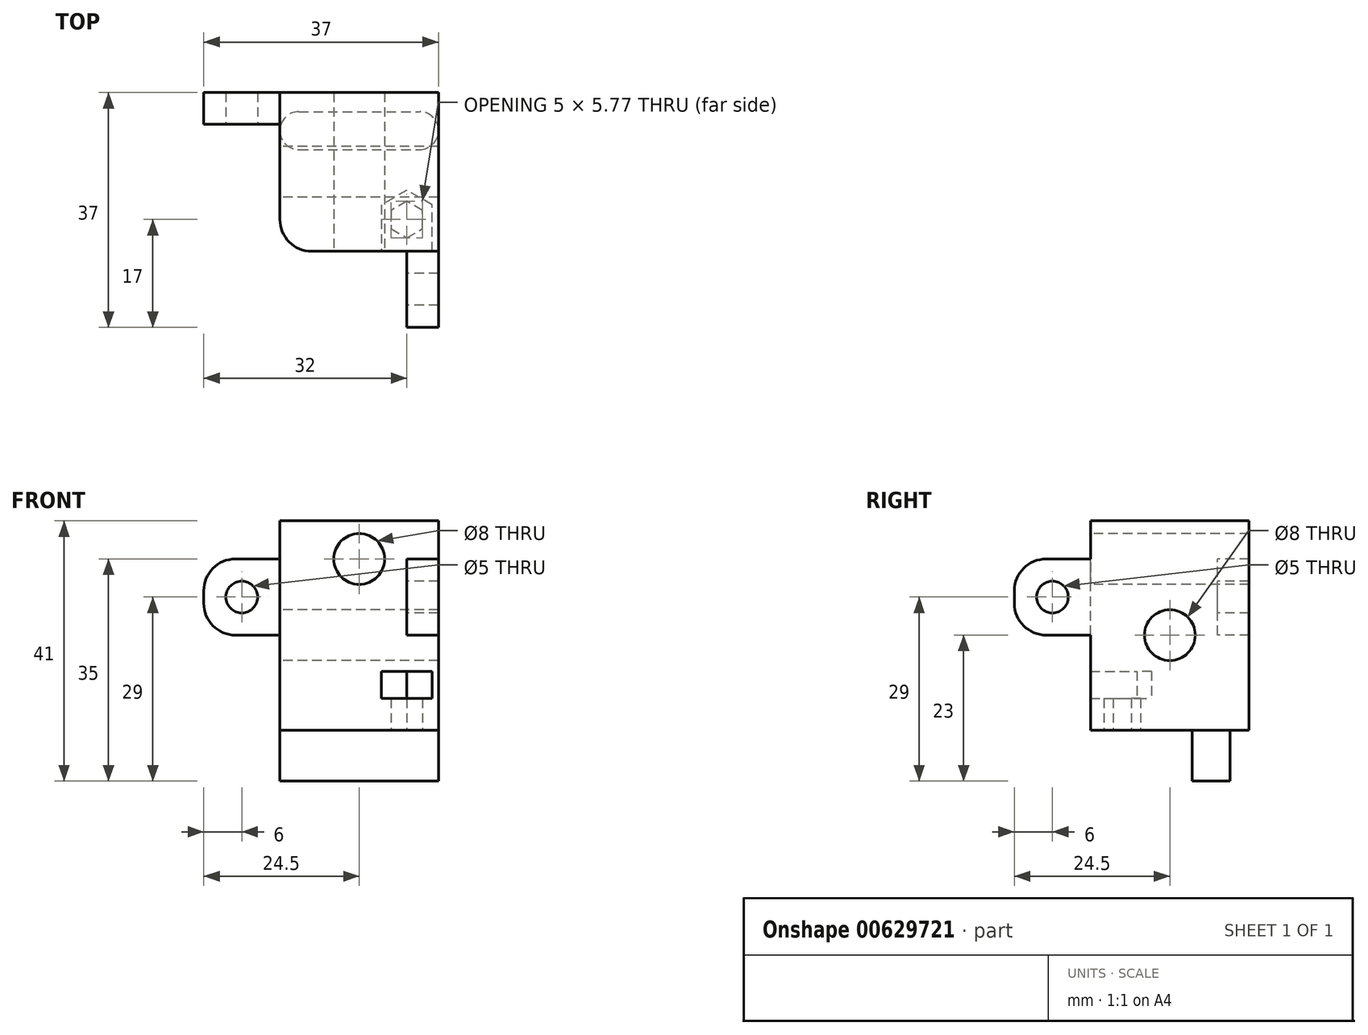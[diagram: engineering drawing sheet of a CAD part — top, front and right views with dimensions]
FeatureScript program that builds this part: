
annotation { "Feature Type Name" : "Feature", "Feature Type Description" : "" }
export const myFeature = defineFeature(function(context is Context, id is Id, definition is map)
    precondition{}
    {
        {
            var Q0;
            Q0=qCreatedBy(makeId("Front.planeOp"),FACE);
            var sketch = newSketch(context, id + "F0", { "sketchPlane" : qUnion([Q0])});
            skLineSegment(sketch, "E0.bottom", {"start": v(0, 0) * mm, "end": v(25, 0) * mm});
            skLineSegment(sketch, "E0.top", {"start": v(0, 45) * mm, "end": v(25, 45) * mm});
            skLineSegment(sketch, "E0.left", {"start": v(0, 0) * mm, "end": v(0, 45) * mm});
            skLineSegment(sketch, "E0.right", {"start": v(25, 0) * mm, "end": v(25, 45) * mm});
            skSolve(sketch);
        }
        {
            var Q0;
            Q0=makeQuery(id+"F0.imprint","IMPRINT",FACE,{"disambiguationData":[TD([[makeQuery(id+"F0.imprint","IMPRINT",EDGE,{"derivedFrom":sQuery(id+"F0.wireOp",EDGE,"E0.bottom")}),1.0]])]});
            extrude(context, id + "F1", {"entities" : qUnion([Q0]), "depth" : 25 * mm});
        }
        {
            var Q0;
            Q0=makeQuery(id+"F1.opExtrude","CAP_FACE",FACE,{"disambiguationData":[OSD([sQuery(id+"F0.wireOp",EDGE,"E0.bottom"),sQuery(id+"F0.wireOp",EDGE,"E0.top"),sQuery(id+"F0.wireOp",EDGE,"E0.left"),sQuery(id+"F0.wireOp",EDGE,"E0.right")])],"isStart":false});
            var sketch = newSketch(context, id + "F2", { "sketchPlane" : qUnion([Q0])});
            skLineSegment(sketch, "E1", {"start": v(12.5, 0) * mm, "end": v(12.5, 37) * mm});
            skCircle(sketch, "E2", {"center": v(12.5, 37) * mm, "radius": 4 * mm});
            skSolve(sketch);
        }
        {
            var Q0;
            Q0=makeQuery(id+"F2.imprint","IMPRINT",FACE,{"disambiguationData":[TD([[makeQuery(id+"F2.imprint","IMPRINT",EDGE,{"derivedFrom":sQuery(id+"F2.wireOp",EDGE,"E2")}),1.0]])]});
            extrude(context, id + "F3", {"entities" : qUnion([Q0]), "operationType" : NewBodyOperationType.REMOVE, "oppositeDirection" : true, "depth" : 25 * mm});
        }
        {
            var Q0;
            Q0=makeQuery(id+"F1.opExtrude","SWEPT_FACE",FACE,{"disambiguationData":[OSD([sQuery(id+"F0.wireOp",EDGE,"E0.left")])]});
            var sketch = newSketch(context, id + "F4", { "sketchPlane" : qUnion([Q0])});
            skLineSegment(sketch, "E3", {"start": v(12.5, 0) * mm, "end": v(12.5, 25) * mm});
            skCircle(sketch, "E4", {"center": v(12.5, 25) * mm, "radius": 4 * mm});
            skSolve(sketch);
        }
        {
            var Q0;
            Q0=makeQuery(id+"F4.imprint","IMPRINT",FACE,{"disambiguationData":[TD([[makeQuery(id+"F4.imprint","IMPRINT",EDGE,{"derivedFrom":sQuery(id+"F4.wireOp",EDGE,"E4")}),1.0]])]});
            extrude(context, id + "F5", {"entities" : qUnion([Q0]), "operationType" : NewBodyOperationType.REMOVE, "oppositeDirection" : true, "depth" : 25 * mm});
        }
        {
            var Q0;
            Q0=makeQuery(id+"F1.opExtrude","SWEPT_FACE",FACE,{"disambiguationData":[OSD([sQuery(id+"F0.wireOp",EDGE,"E0.left")])]});
            var sketch = newSketch(context, id + "F6", { "sketchPlane" : qUnion([Q0])});
            skLineSegment(sketch, "E5.bottom", {"start": v(0, 25) * mm, "end": v(5, 25) * mm});
            skLineSegment(sketch, "E5.top", {"start": v(0, 37) * mm, "end": v(5, 37) * mm});
            skLineSegment(sketch, "E5.left", {"start": v(0, 25) * mm, "end": v(0, 37) * mm});
            skLineSegment(sketch, "E5.right", {"start": v(5, 25) * mm, "end": v(5, 37) * mm});
            skSolve(sketch);
        }
        {
            var Q0;
            Q0=makeQuery(id+"F6.imprint","IMPRINT",FACE,{"disambiguationData":[TD([[makeQuery(id+"F6.imprint","IMPRINT",EDGE,{"derivedFrom":sQuery(id+"F6.wireOp",EDGE,"E5.bottom")}),1.0]])]});
            extrude(context, id + "F7", {"entities" : qUnion([Q0]), "operationType" : NewBodyOperationType.ADD, "depth" : 12 * mm});
        }
        {
            var Q0;
            Q0=makeQuery(id+"F7.opExtrude","SWEPT_FACE",FACE,{"disambiguationData":[OSD([sQuery(id+"F6.wireOp",EDGE,"E5.right")])]});
            var sketch = newSketch(context, id + "F8", { "sketchPlane" : qUnion([Q0])});
            skLineSegment(sketch, "E6", {"start": v(-6, 25) * mm, "end": v(-6, 37) * mm});
            skCircle(sketch, "E7", {"center": v(-6, 31) * mm, "radius": 2.5 * mm});
            skSolve(sketch);
        }
        {
            var Q0;
            {var subQ0=sQuery(id+"F8.wireOp",EDGE,"E7");var subQ1=sQuery(id+"F8.wireOp",EDGE,"E6");var subQ2=makeQuery(id+"F8.imprint","INTERSECT",VERTEX,{"disambiguationData":[OD(0.0)],"derivedFrom":[subQ1,subQ0]});Q0=makeQuery(id+"F8.imprint","IMPRINT",FACE,{"disambiguationData":[TD([[makeQuery(id+"F8.imprint","IMPRINT",EDGE,{"disambiguationData":[TD([[subQ2,-1.0]])],"derivedFrom":subQ1}),1.0]])]});}
            var Q1;
            {var subQ0=sQuery(id+"F8.wireOp",EDGE,"E7");var subQ1=sQuery(id+"F8.wireOp",EDGE,"E6");var subQ2=makeQuery(id+"F8.imprint","INTERSECT",VERTEX,{"disambiguationData":[OD(0.0)],"derivedFrom":[subQ1,subQ0]});Q1=makeQuery(id+"F8.imprint","IMPRINT",FACE,{"disambiguationData":[TD([[makeQuery(id+"F8.imprint","IMPRINT",EDGE,{"disambiguationData":[TD([[subQ2,-1.0]])],"derivedFrom":subQ1}),-1.0]])]});}
            extrude(context, id + "F9", {"entities" : qUnion([Q0, Q1]), "operationType" : NewBodyOperationType.REMOVE, "oppositeDirection" : true, "depth" : 25 * mm});
        }
        {
            var Q0;
            Q0=makeQuery(id+"F7.opExtrude","CAP_EDGE",EDGE,{"disambiguationData":[OSD([sQuery(id+"F6.wireOp",EDGE,"E5.top")])],"isStart":false});
            var Q1;
            Q1=makeQuery(id+"F7.opExtrude","CAP_EDGE",EDGE,{"disambiguationData":[OSD([sQuery(id+"F6.wireOp",EDGE,"E5.bottom")])],"isStart":false});
            var Q2;
            Q2=makeQuery(id+"F7.opExtrude","CAP_EDGE",EDGE,{"disambiguationData":[OSD([sQuery(id+"F6.wireOp",EDGE,"E5.top")])],"isStart":true});
            fillet(context, id + "F10", {"entities" : qUnion([Q0, Q1, Q2]), "radius" : 5 * mm, "tangentPropagation" : true, "allowEdgeOverflow" : false});
        }
        {
            var Q0;
            Q0=makeQuery(id+"F1.opExtrude","CAP_FACE",FACE,{"disambiguationData":[OSD([sQuery(id+"F0.wireOp",EDGE,"E0.bottom"),sQuery(id+"F0.wireOp",EDGE,"E0.top"),sQuery(id+"F0.wireOp",EDGE,"E0.left"),sQuery(id+"F0.wireOp",EDGE,"E0.right")])],"isStart":false});
            var sketch = newSketch(context, id + "F11", { "sketchPlane" : qUnion([Q0])});
            skLineSegment(sketch, "E8.bottom", {"start": v(25, 25) * mm, "end": v(20, 25) * mm});
            skLineSegment(sketch, "E8.top", {"start": v(25, 37) * mm, "end": v(20, 37) * mm});
            skLineSegment(sketch, "E8.left", {"start": v(25, 25) * mm, "end": v(25, 37) * mm});
            skLineSegment(sketch, "E8.right", {"start": v(20, 25) * mm, "end": v(20, 37) * mm});
            skSolve(sketch);
        }
        {
            var Q0;
            Q0=makeQuery(id+"F11.imprint","IMPRINT",FACE,{"disambiguationData":[TD([[makeQuery(id+"F11.imprint","IMPRINT",EDGE,{"derivedFrom":sQuery(id+"F11.wireOp",EDGE,"E8.bottom")}),-1.0]])]});
            extrude(context, id + "F12", {"entities" : qUnion([Q0]), "operationType" : NewBodyOperationType.ADD, "depth" : 12 * mm});
        }
        {
            var Q0;
            Q0=makeQuery(id+"F12.opExtrude","SWEPT_FACE",FACE,{"disambiguationData":[OSD([sQuery(id+"F11.wireOp",EDGE,"E8.right")])]});
            var sketch = newSketch(context, id + "F13", { "sketchPlane" : qUnion([Q0])});
            skLineSegment(sketch, "E9", {"start": v(31, 25) * mm, "end": v(31, 37) * mm});
            skCircle(sketch, "E10", {"center": v(31, 31) * mm, "radius": 2.5 * mm});
            skSolve(sketch);
        }
        {
            var Q0;
            {var subQ0=sQuery(id+"F13.wireOp",EDGE,"E10");var subQ1=sQuery(id+"F13.wireOp",EDGE,"E9");var subQ2=makeQuery(id+"F13.imprint","INTERSECT",VERTEX,{"disambiguationData":[OD(0.0)],"derivedFrom":[subQ1,subQ0]});Q0=makeQuery(id+"F13.imprint","IMPRINT",FACE,{"disambiguationData":[TD([[makeQuery(id+"F13.imprint","IMPRINT",EDGE,{"disambiguationData":[TD([[subQ2,-1.0]])],"derivedFrom":subQ1}),1.0]])]});}
            var Q1;
            {var subQ0=sQuery(id+"F13.wireOp",EDGE,"E10");var subQ1=sQuery(id+"F13.wireOp",EDGE,"E9");var subQ2=makeQuery(id+"F13.imprint","INTERSECT",VERTEX,{"disambiguationData":[OD(0.0)],"derivedFrom":[subQ1,subQ0]});Q1=makeQuery(id+"F13.imprint","IMPRINT",FACE,{"disambiguationData":[TD([[makeQuery(id+"F13.imprint","IMPRINT",EDGE,{"disambiguationData":[TD([[subQ2,-1.0]])],"derivedFrom":subQ1}),-1.0]])]});}
            extrude(context, id + "F14", {"entities" : qUnion([Q0, Q1]), "operationType" : NewBodyOperationType.REMOVE, "oppositeDirection" : true, "depth" : 25 * mm});
        }
        {
            var Q0;
            Q0=makeQuery(id+"F12.opExtrude","CAP_EDGE",EDGE,{"disambiguationData":[OSD([sQuery(id+"F11.wireOp",EDGE,"E8.top")])],"isStart":false});
            var Q1;
            Q1=makeQuery(id+"F12.opExtrude","CAP_EDGE",EDGE,{"disambiguationData":[OSD([sQuery(id+"F11.wireOp",EDGE,"E8.bottom")])],"isStart":false});
            var Q2;
            Q2=makeQuery(id+"F12.opExtrude","CAP_EDGE",EDGE,{"disambiguationData":[OSD([sQuery(id+"F11.wireOp",EDGE,"E8.bottom")])],"isStart":true});
            fillet(context, id + "F15", {"entities" : qUnion([Q0, Q1, Q2]), "radius" : 5 * mm, "tangentPropagation" : true, "allowEdgeOverflow" : false});
        }
        {
            var Q0;
            Q0=makeQuery(id+"F1.opExtrude","SWEPT_FACE",FACE,{"disambiguationData":[OSD([sQuery(id+"F0.wireOp",EDGE,"E0.left")])]});
            var sketch = newSketch(context, id + "F16", { "sketchPlane" : qUnion([Q0])});
            skLineSegment(sketch, "E11.bottom", {"start": v(25, 4) * mm, "end": v(6, 4) * mm});
            skLineSegment(sketch, "E11.top", {"start": v(25, 10) * mm, "end": v(6, 10) * mm});
            skLineSegment(sketch, "E11.left", {"start": v(25, 4) * mm, "end": v(25, 10) * mm});
            skLineSegment(sketch, "E11.right", {"start": v(6, 4) * mm, "end": v(6, 10) * mm});
            skSolve(sketch);
        }
        {
            var Q0;
            Q0=makeQuery(id+"F16.imprint","IMPRINT",FACE,{"disambiguationData":[TD([[makeQuery(id+"F16.imprint","IMPRINT",EDGE,{"derivedFrom":sQuery(id+"F16.wireOp",EDGE,"E11.bottom")}),-1.0]])]});
            extrude(context, id + "F17", {"entities" : qUnion([Q0]), "operationType" : NewBodyOperationType.REMOVE, "oppositeDirection" : true, "depth" : 19 * mm});
        }
        {
            var Q0;
            Q0=makeQuery(id+"F1.opExtrude","SWEPT_FACE",FACE,{"disambiguationData":[OSD([sQuery(id+"F0.wireOp",EDGE,"E0.bottom")])]});
            var sketch = newSketch(context, id + "F18", { "sketchPlane" : qUnion([Q0])});
            skCircle(sketch, "E12.cCircle", {"center": v(20, 20) * mm, "radius": 2.5 * mm, "construction": true});
            skLineSegment(sketch, "E12.0", {"start": v(17.5, 18.56) * mm, "end": v(17.5, 21.44) * mm});
            skLineSegment(sketch, "E12.1", {"start": v(17.5, 21.44) * mm, "end": v(20, 22.89) * mm});
            skLineSegment(sketch, "E12.2", {"start": v(20, 22.89) * mm, "end": v(22.5, 21.44) * mm});
            skLineSegment(sketch, "E12.3", {"start": v(22.5, 21.44) * mm, "end": v(22.5, 18.56) * mm});
            skLineSegment(sketch, "E12.4", {"start": v(22.5, 18.56) * mm, "end": v(20, 17.11) * mm});
            skLineSegment(sketch, "E12.5", {"start": v(20, 17.11) * mm, "end": v(17.5, 18.56) * mm});
            skPoint(sketch, "E12.0.midPoint", {"position": v(17.5, 20) * mm});
            skLineSegment(sketch, "E13", {"start": v(20, 20) * mm, "end": v(20, 25) * mm});
            skLineSegment(sketch, "E14", {"start": v(20, 20) * mm, "end": v(25, 20) * mm});
            skSolve(sketch);
        }
        {
            var Q0;
            {var subQ3=sQuery(id+"F18.wireOp",EDGE,"E12.0");Q0=makeQuery(id+"F18.imprint","IMPRINT",FACE,{"disambiguationData":[TD([[makeQuery(id+"F18.imprint","IMPRINT",EDGE,{"derivedFrom":subQ3}),-1.0]])]});}
            var Q1;
            {var subQ0=sQuery(id+"F18.wireOp",EDGE,"E12.2");Q1=makeQuery(id+"F18.imprint","IMPRINT",FACE,{"disambiguationData":[TD([[makeQuery(id+"F18.imprint","IMPRINT",EDGE,{"derivedFrom":subQ0}),-1.0]])]});}
            extrude(context, id + "F19", {"entities" : qUnion([Q0, Q1]), "operationType" : NewBodyOperationType.REMOVE, "oppositeDirection" : true, "depth" : 12 * mm});
        }
        {
            var Q0;
            Q0=makeQuery(id+"F17.boolean.opBoolean","COPY",EDGE,{"derivedFrom":makeQuery(id+"F17.opExtrude","CAP_EDGE",EDGE,{"disambiguationData":[OSD([sQuery(id+"F16.wireOp",EDGE,"E11.right")])],"isStart":false})});
            fillet(context, id + "F20", {"entities" : qUnion([Q0]), "radius" : 5 * mm, "tangentPropagation" : true, "allowEdgeOverflow" : false});
        }
        {
            var Q0;
            {var subQ0=sQuery(id+"F0.wireOp",EDGE,"E0.bottom");var subQ1=sQuery(id+"F0.wireOp",EDGE,"E0.left");Q0=makeQuery(id+"F17.boolean.opBoolean","SPLIT",EDGE,{"disambiguationData":[TD([makeQuery(id+"F1.opExtrude","SWEPT_FACE",FACE,{"disambiguationData":[OSD([subQ0])]})])],"derivedFrom":makeQuery(id+"F1.opExtrude","CAP_EDGE",EDGE,{"disambiguationData":[OSD([subQ1])],"isStart":false})});}
            var Q1;
            {var subQ0=sQuery(id+"F0.wireOp",EDGE,"E0.left");var subQ1=sQuery(id+"F0.wireOp",EDGE,"E0.top");Q1=makeQuery(id+"F17.boolean.opBoolean","SPLIT",EDGE,{"disambiguationData":[TD([makeQuery(id+"F1.opExtrude","SWEPT_FACE",FACE,{"disambiguationData":[OSD([subQ1])]})])],"derivedFrom":makeQuery(id+"F1.opExtrude","CAP_EDGE",EDGE,{"disambiguationData":[OSD([subQ0])],"isStart":false})});}
            fillet(context, id + "F21", {"entities" : qUnion([Q0, Q1]), "radius" : 5 * mm, "tangentPropagation" : true, "allowEdgeOverflow" : false});
        }
        {
            var Q0;
            Q0=makeQuery(id+"F1.opExtrude","SWEPT_FACE",FACE,{"disambiguationData":[OSD([sQuery(id+"F0.wireOp",EDGE,"E0.top")])]});
            extrude(context, id + "F22", {"entities" : qUnion([Q0]), "operationType" : NewBodyOperationType.REMOVE, "oppositeDirection" : true, "depth" : 2 * mm});
        }
        {
            var Q0;
            Q0=makeQuery(id+"F1.opExtrude","CAP_FACE",FACE,{"disambiguationData":[OSD([sQuery(id+"F0.wireOp",EDGE,"E0.bottom"),sQuery(id+"F0.wireOp",EDGE,"E0.top"),sQuery(id+"F0.wireOp",EDGE,"E0.left"),sQuery(id+"F0.wireOp",EDGE,"E0.right")])],"isStart":false});
            var sketch = newSketch(context, id + "F23", { "sketchPlane" : qUnion([Q0])});
            skLineSegment(sketch, "E15", {"start": v(19, 10) * mm, "end": v(25, 10) * mm});
            skLineSegment(sketch, "E16.bottom", {"start": v(25, 10) * mm, "end": v(0, 10) * mm});
            skLineSegment(sketch, "E16.top", {"start": v(25, 0) * mm, "end": v(0, 0) * mm});
            skLineSegment(sketch, "E16.left", {"start": v(25, 10) * mm, "end": v(25, 0) * mm});
            skLineSegment(sketch, "E16.right", {"start": v(0, 10) * mm, "end": v(0, 0) * mm});
            skSolve(sketch);
        }
        {
            var Q0;
            {var subQ2=sQuery(id+"F23.wireOp",EDGE,"E16.left");Q0=makeQuery(id+"F23.imprint","IMPRINT",FACE,{"disambiguationData":[TD([[makeQuery(id+"F23.imprint","IMPRINT",EDGE,{"derivedFrom":subQ2}),1.0]])]});}
            var Q1;
            {var subQ0=sQuery(id+"F23.wireOp",EDGE,"E16.right");Q1=makeQuery(id+"F23.imprint","IMPRINT",FACE,{"disambiguationData":[TD([[makeQuery(id+"F23.imprint","IMPRINT",EDGE,{"derivedFrom":subQ0}),1.0]])]});}
            extrude(context, id + "F24", {"entities" : qUnion([Q0, Q1]), "operationType" : NewBodyOperationType.REMOVE, "oppositeDirection" : true, "depth" : 25 * mm});
        }
        {
            var Q0;
            Q0=makeQuery(id+"F24.boolean.opBoolean","MERGE",FACE,{"derivedFrom":[makeQuery(id+"F17.boolean.opBoolean","COPY",FACE,{"derivedFrom":makeQuery(id+"F17.opExtrude","SWEPT_FACE",FACE,{"disambiguationData":[OSD([sQuery(id+"F16.wireOp",EDGE,"E11.top")])]})}),makeQuery(id+"F24.opExtrude","SWEPT_FACE",FACE,{"disambiguationData":[OSD([sQuery(id+"F23.wireOp",EDGE,"E16.bottom")])]})]});
            cPlane(context, id + "F25", {"entities" : qUnion([Q0]), "cplaneType" : CPlaneType.OFFSET, "offset" : 5 * mm, "oppositeDirection" : true, "width" : 150 * mm, "height" : 150 * mm});
        }
        {
            var Q0;
            Q0=qCreatedBy(id+"F25.planeOp",FACE);
            var sketch = newSketch(context, id + "F26", { "sketchPlane" : qUnion([Q0])});
            skLineSegment(sketch, "E17", {"start": v(0, 0) * mm, "end": v(25, 0) * mm});
            skLineSegment(sketch, "E18", {"start": v(20, 20) * mm, "end": v(20, 15.06) * mm});
            skLineSegment(sketch, "E19", {"start": v(20, 15.06) * mm, "end": v(20, 24.25) * mm});
            skCircle(sketch, "E20.cCircle", {"center": v(20, 20) * mm, "radius": 4 * mm, "construction": true});
            skLineSegment(sketch, "E20.0", {"start": v(24, 22.3) * mm, "end": v(24, 17.7) * mm});
            skLineSegment(sketch, "E20.1", {"start": v(24, 17.7) * mm, "end": v(20, 15.38) * mm});
            skLineSegment(sketch, "E20.2", {"start": v(20, 15.38) * mm, "end": v(16, 17.7) * mm});
            skLineSegment(sketch, "E20.3", {"start": v(16, 17.7) * mm, "end": v(16, 22.3) * mm});
            skLineSegment(sketch, "E20.4", {"start": v(16, 22.3) * mm, "end": v(20, 24.62) * mm});
            skLineSegment(sketch, "E20.5", {"start": v(20, 24.62) * mm, "end": v(24, 22.3) * mm});
            skPoint(sketch, "E20.0.midPoint", {"position": v(24, 20) * mm});
            skLineSegment(sketch, "E21", {"start": v(16, 22.3) * mm, "end": v(16, 30.3) * mm});
            skLineSegment(sketch, "E22", {"start": v(16, 30.3) * mm, "end": v(24, 30.3) * mm});
            skLineSegment(sketch, "E23", {"start": v(24, 30.3) * mm, "end": v(24, 22.3) * mm});
            skSolve(sketch);
        }
        {
            var Q0;
            Q0=qSketchRegion(id+"F26",true);
            extrude(context, id + "F27", {"entities" : qUnion([Q0]), "operationType" : NewBodyOperationType.REMOVE, "oppositeDirection" : true, "depth" : 4.3 * mm});
        }
        {
            var Q0;
            Q0=makeQuery(id+"F19.boolean.opBoolean","COPY",FACE,{"derivedFrom":makeQuery(id+"F19.opExtrude","CAP_FACE",FACE,{"disambiguationData":[OSD([sQuery(id+"F18.wireOp",EDGE,"E12.0"),sQuery(id+"F18.wireOp",EDGE,"E12.1"),sQuery(id+"F18.wireOp",EDGE,"E12.2"),sQuery(id+"F18.wireOp",EDGE,"E12.3"),sQuery(id+"F18.wireOp",EDGE,"E12.4"),sQuery(id+"F18.wireOp",EDGE,"E12.5")])],"isStart":false})});
            extrude(context, id + "F28", {"entities" : qUnion([Q0]), "operationType" : NewBodyOperationType.REMOVE, "oppositeDirection" : true, "depth" : 5 * mm});
        }
        {
            var Q0;
            Q0=makeQuery(id+"F24.boolean.opBoolean","MERGE",FACE,{"derivedFrom":[makeQuery(id+"F17.boolean.opBoolean","COPY",FACE,{"derivedFrom":makeQuery(id+"F17.opExtrude","SWEPT_FACE",FACE,{"disambiguationData":[OSD([sQuery(id+"F16.wireOp",EDGE,"E11.top")])]})}),makeQuery(id+"F24.opExtrude","SWEPT_FACE",FACE,{"disambiguationData":[OSD([sQuery(id+"F23.wireOp",EDGE,"E16.bottom")])]})]});
            var sketch = newSketch(context, id + "F29", { "sketchPlane" : qUnion([Q0])});
            skLineSegment(sketch, "E24.bottom", {"start": v(3, 3) * mm, "end": v(22, 3) * mm});
            skLineSegment(sketch, "E24.top", {"start": v(3, 9) * mm, "end": v(22, 9) * mm});
            skLineSegment(sketch, "E24.left", {"start": v(0, 6) * mm, "end": v(0, 6) * mm});
            skLineSegment(sketch, "E24.right", {"start": v(25, 6) * mm, "end": v(25, 6) * mm});
            skPoint(sketch, "E25.visualSharp", {"position": v(0, 3) * mm});
            skArc(sketch, "E25.filletArc", {"start": v(0, 6) * mm, "mid": v(0.88, 3.88) * mm, "end": v(3, 3) * mm});
            skPoint(sketch, "E26.visualSharp", {"position": v(0, 9) * mm});
            skArc(sketch, "E26.filletArc", {"start": v(3, 9) * mm, "mid": v(0.88, 8.12) * mm, "end": v(0, 6) * mm});
            skPoint(sketch, "E27.visualSharp", {"position": v(25, 9) * mm});
            skArc(sketch, "E27.filletArc", {"start": v(25, 6) * mm, "mid": v(24.12, 8.12) * mm, "end": v(22, 9) * mm});
            skPoint(sketch, "E28.visualSharp", {"position": v(25, 3) * mm});
            skArc(sketch, "E28.filletArc", {"start": v(22, 3) * mm, "mid": v(24.12, 3.88) * mm, "end": v(25, 6) * mm});
            skSolve(sketch);
        }
        {
            var Q0;
            Q0=makeQuery(id+"F29.imprint","IMPRINT",FACE,{"disambiguationData":[TD([[makeQuery(id+"F29.imprint","IMPRINT",EDGE,{"derivedFrom":sQuery(id+"F29.wireOp",EDGE,"E24.bottom")}),1.0]])]});
            extrude(context, id + "F30", {"entities" : qUnion([Q0]), "operationType" : NewBodyOperationType.ADD, "depth" : 8 * mm});
        }
    });
